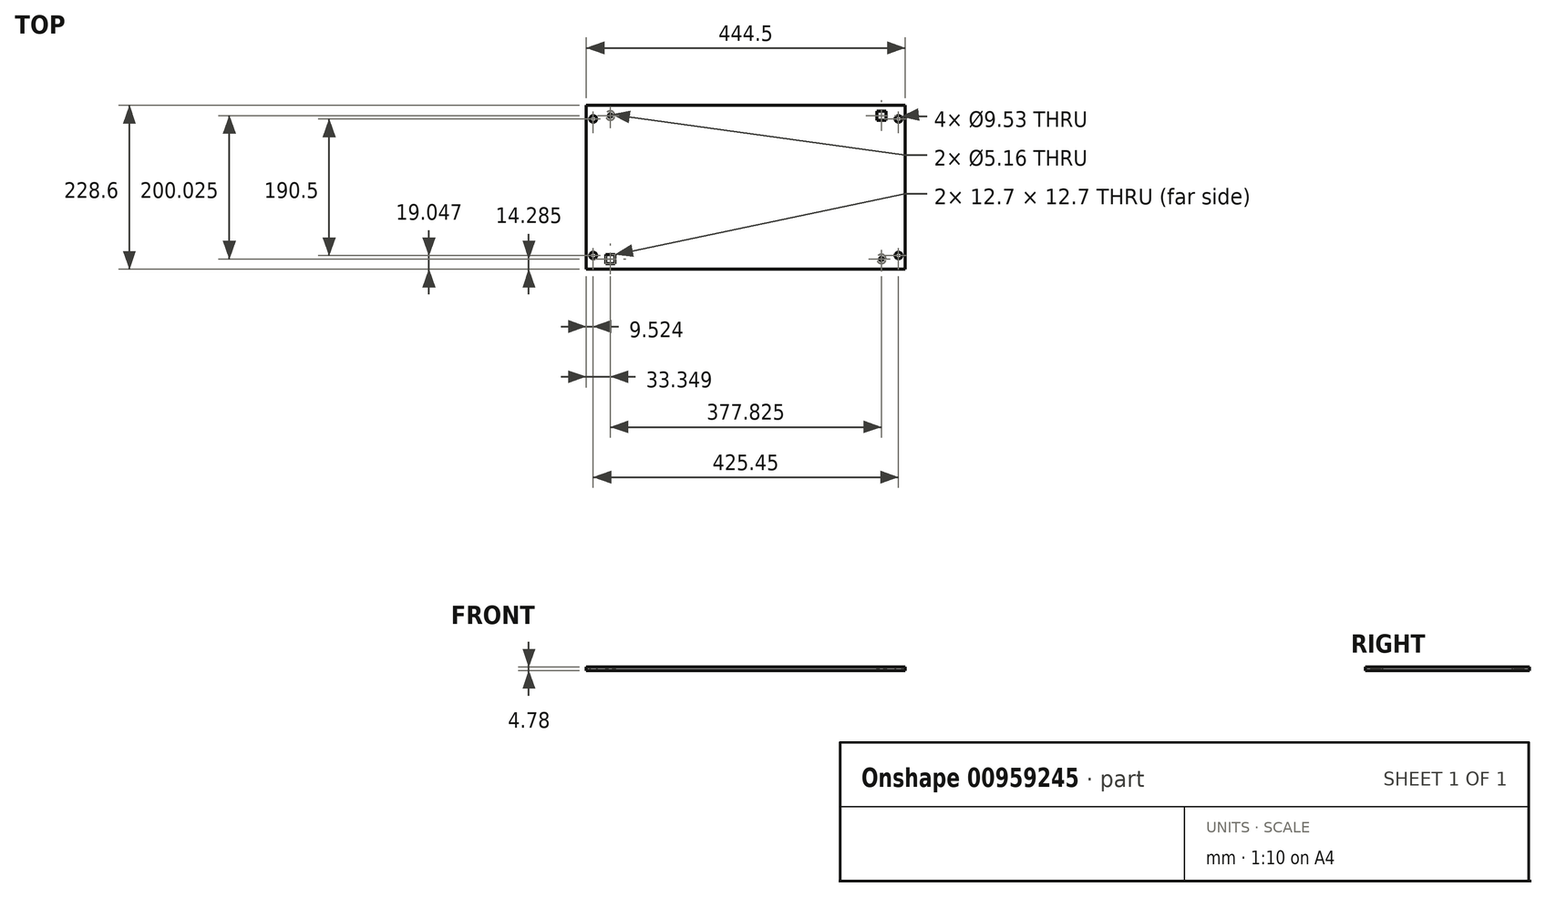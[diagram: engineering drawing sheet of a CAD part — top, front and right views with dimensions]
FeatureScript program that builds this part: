
annotation { "Feature Type Name" : "Feature", "Feature Type Description" : "" }
export const myFeature = defineFeature(function(context is Context, id is Id, definition is map)
    precondition{}
    {
        {
            var Q0;
            Q0=qCreatedBy(makeId("Top.planeOp"),FACE);
            var sketch = newSketch(context, id + "F0", { "sketchPlane" : qUnion([Q0])});
            skLineSegment(sketch, "E0.bottom", {"start": v(-225.5, 123.74) * mm, "end": v(180.9, 123.74) * mm});
            skLineSegment(sketch, "E0.top", {"start": v(-225.5, -104.86) * mm, "end": v(180.9, -104.86) * mm});
            skLineSegment(sketch, "E0.left", {"start": v(-225.5, 123.74) * mm, "end": v(-225.5, -104.86) * mm});
            skLineSegment(sketch, "E0.right", {"start": v(180.9, 123.74) * mm, "end": v(180.9, -104.86) * mm});
            skLineSegment(sketch, "E1.bottom", {"start": v(-220.72, 118.97) * mm, "end": v(176.16, 118.97) * mm});
            skLineSegment(sketch, "E1.top", {"start": v(-220.72, -100.1) * mm, "end": v(176.16, -100.1) * mm});
            skLineSegment(sketch, "E1.left", {"start": v(-220.72, 118.97) * mm, "end": v(-220.72, -100.1) * mm});
            skLineSegment(sketch, "E1.right", {"start": v(176.16, 118.97) * mm, "end": v(176.16, -100.1) * mm});
            skLineSegment(sketch, "E2.bottom", {"start": v(-225.5, 123.74) * mm, "end": v(-244.54, 123.74) * mm});
            skLineSegment(sketch, "E2.top", {"start": v(-225.5, -104.86) * mm, "end": v(-244.54, -104.86) * mm});
            skLineSegment(sketch, "E2.right", {"start": v(-244.54, 123.74) * mm, "end": v(-244.54, -104.86) * mm});
            skLineSegment(sketch, "E3.bottom", {"start": v(180.9, 123.74) * mm, "end": v(199.96, 123.74) * mm});
            skLineSegment(sketch, "E3.top", {"start": v(180.9, -104.86) * mm, "end": v(199.96, -104.86) * mm});
            skLineSegment(sketch, "E3.right", {"start": v(199.96, 123.74) * mm, "end": v(199.96, -104.86) * mm});
            skCircle(sketch, "E4", {"center": v(-235.02, 104.69) * mm, "radius": 4.76 * mm});
            skCircle(sketch, "E5", {"center": v(-235.02, -85.81) * mm, "radius": 4.76 * mm});
            skCircle(sketch, "E6", {"center": v(190.43, 104.69) * mm, "radius": 4.76 * mm});
            skCircle(sketch, "E7", {"center": v(190.43, -85.81) * mm, "radius": 4.76 * mm});
            skLineSegment(sketch, "E8.bottom", {"start": v(-217.54, -84.23) * mm, "end": v(-204.84, -84.23) * mm});
            skLineSegment(sketch, "E8.top", {"start": v(-217.54, -96.93) * mm, "end": v(-204.84, -96.93) * mm});
            skLineSegment(sketch, "E8.left", {"start": v(-217.54, -84.23) * mm, "end": v(-217.54, -96.93) * mm});
            skLineSegment(sketch, "E8.right", {"start": v(-204.84, -84.23) * mm, "end": v(-204.84, -96.93) * mm});
            skLineSegment(sketch, "E9.bottom", {"start": v(160.28, -84.23) * mm, "end": v(172.98, -84.23) * mm});
            skLineSegment(sketch, "E9.top", {"start": v(160.28, -96.93) * mm, "end": v(172.98, -96.93) * mm});
            skLineSegment(sketch, "E9.left", {"start": v(160.28, -84.23) * mm, "end": v(160.28, -96.93) * mm});
            skLineSegment(sketch, "E9.right", {"start": v(172.98, -84.23) * mm, "end": v(172.98, -96.93) * mm});
            skLineSegment(sketch, "E10.bottom", {"start": v(160.28, 115.8) * mm, "end": v(172.98, 115.8) * mm});
            skLineSegment(sketch, "E10.top", {"start": v(160.28, 103.1) * mm, "end": v(172.98, 103.1) * mm});
            skLineSegment(sketch, "E10.left", {"start": v(160.28, 115.8) * mm, "end": v(160.28, 103.1) * mm});
            skLineSegment(sketch, "E10.right", {"start": v(172.98, 115.8) * mm, "end": v(172.98, 103.1) * mm});
            skLineSegment(sketch, "E11.bottom", {"start": v(-217.54, 115.8) * mm, "end": v(-204.84, 115.8) * mm});
            skLineSegment(sketch, "E11.top", {"start": v(-217.54, 103.1) * mm, "end": v(-204.84, 103.1) * mm});
            skLineSegment(sketch, "E11.left", {"start": v(-217.54, 115.8) * mm, "end": v(-217.54, 103.1) * mm});
            skLineSegment(sketch, "E11.right", {"start": v(-204.84, 115.8) * mm, "end": v(-204.84, 103.1) * mm});
            skCircle(sketch, "E12", {"center": v(-211.2, 109.45) * mm, "radius": 2.58 * mm});
            skCircle(sketch, "E13", {"center": v(166.63, 109.45) * mm, "radius": 2.58 * mm});
            skCircle(sketch, "E14", {"center": v(166.63, -90.58) * mm, "radius": 2.58 * mm});
            skCircle(sketch, "E15", {"center": v(-211.2, -90.58) * mm, "radius": 2.58 * mm});
            skSolve(sketch);
        }
        {
            var Q0;
            Q0 = qSketchRegion(id + "F0", true);
            var Q1;
            Q1=makeQuery(id+"F0.imprint","IMPRINT",FACE,{"disambiguationData":[TD([[makeQuery(id+"F0.imprint","IMPRINT",EDGE,{"derivedFrom":sQuery(id+"F0.wireOp",EDGE,"E1.bottom")}),-1.0]])]});
            var Q2;
            Q2=makeQuery(id+"F0.imprint","IMPRINT",FACE,{"disambiguationData":[TD([[makeQuery(id+"F0.imprint","IMPRINT",EDGE,{"derivedFrom":sQuery(id+"F0.wireOp",EDGE,"E11.bottom")}),-1.0]])]});
            var Q3;
            Q3=makeQuery(id+"F0.imprint","IMPRINT",FACE,{"disambiguationData":[TD([[makeQuery(id+"F0.imprint","IMPRINT",EDGE,{"derivedFrom":sQuery(id+"F0.wireOp",EDGE,"E8.bottom")}),-1.0]])]});
            var Q4;
            Q4=makeQuery(id+"F0.imprint","IMPRINT",FACE,{"disambiguationData":[TD([[makeQuery(id+"F0.imprint","IMPRINT",EDGE,{"derivedFrom":sQuery(id+"F0.wireOp",EDGE,"E9.bottom")}),-1.0]])]});
            var Q5;
            Q5=makeQuery(id+"F0.imprint","IMPRINT",FACE,{"disambiguationData":[TD([[makeQuery(id+"F0.imprint","IMPRINT",EDGE,{"derivedFrom":sQuery(id+"F0.wireOp",EDGE,"E10.bottom")}),-1.0]])]});
            extrude(context, id + "F1", {"entities" : qUnion([Q0, Q1, Q2, Q3, Q4, Q5]), "depth" : 4.78 * mm, "offsetDistance" : 25.4 * mm});
        }
        {
            var Q0;
            Q0=makeQuery(id+"F1.opExtrude","CAP_EDGE",EDGE,{"disambiguationData":[OSD([sQuery(id+"F0.wireOp",EDGE,"E15")])],"isStart":true});
            var Q1;
            Q1=makeQuery(id+"F1.opExtrude","CAP_EDGE",EDGE,{"disambiguationData":[OSD([sQuery(id+"F0.wireOp",EDGE,"E14")])],"isStart":true});
            var Q2;
            Q2=makeQuery(id+"F1.opExtrude","CAP_EDGE",EDGE,{"disambiguationData":[OSD([sQuery(id+"F0.wireOp",EDGE,"E13")])],"isStart":true});
            var Q3;
            Q3=makeQuery(id+"F1.opExtrude","CAP_EDGE",EDGE,{"disambiguationData":[OSD([sQuery(id+"F0.wireOp",EDGE,"E12")])],"isStart":true});
            chamfer(context, id + "F2", {"entities" : qUnion([Q0, Q1, Q2, Q3]), "width" : 3.8 * mm, "tangentPropagation" : true});
        }
    });
